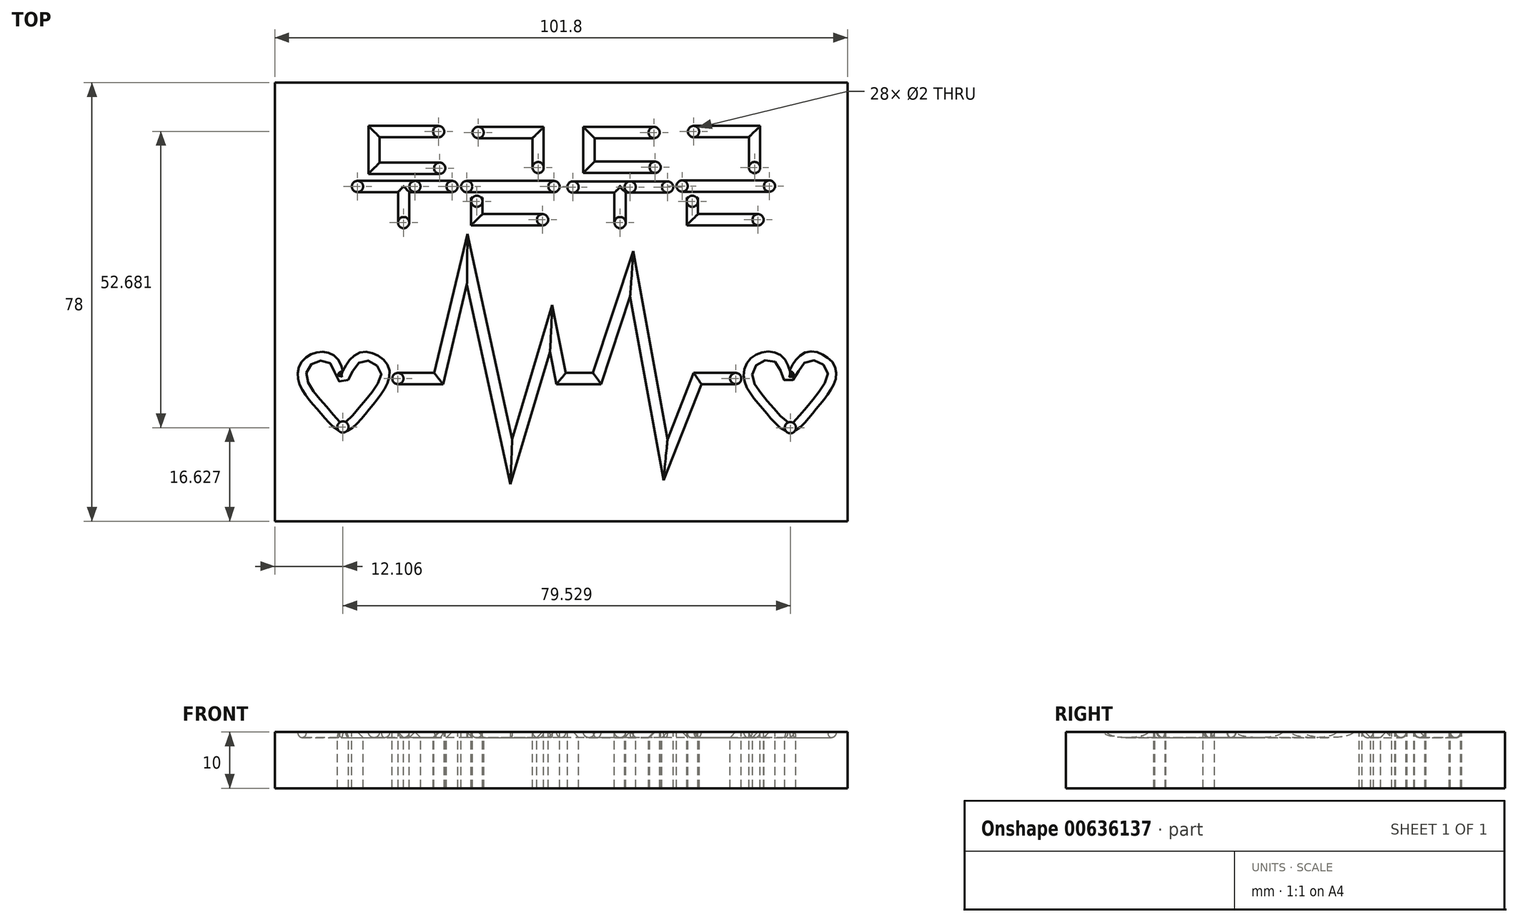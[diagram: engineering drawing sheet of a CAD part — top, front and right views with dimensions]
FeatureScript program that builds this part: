
annotation { "Feature Type Name" : "Feature", "Feature Type Description" : "" }
export const myFeature = defineFeature(function(context is Context, id is Id, definition is map)
    precondition{}
    {
        {
            var Q0;
            Q0=qCreatedBy(makeId("Top.planeOp"),FACE);
            var sketch = newSketch(context, id + "F0", { "sketchPlane" : qUnion([Q0])});
            skLineSegment(sketch, "E0.bottom", {"start": v(50.9, 39) * mm, "end": v(-50.9, 39) * mm});
            skLineSegment(sketch, "E0.top", {"start": v(50.9, -39) * mm, "end": v(-50.9, -39) * mm});
            skLineSegment(sketch, "E0.left", {"start": v(50.9, 39) * mm, "end": v(50.9, -39) * mm});
            skLineSegment(sketch, "E0.right", {"start": v(-50.9, 39) * mm, "end": v(-50.9, -39) * mm});
            skPoint(sketch, "E0.middle", {"position": v(0, 0) * mm});
            skSolve(sketch);
        }
        {
            var Q0;
            Q0 = qSketchRegion(id + "F0", true);
            extrude(context, id + "F1", {"entities" : qUnion([Q0]), "oppositeDirection" : true, "depth" : 10 * mm, "offsetDistance" : 25 * mm});
        }
        {
            var Q0;
            Q0=makeQuery(id+"F1.opExtrude","CAP_FACE",FACE,{"disambiguationData":[OSD([sQuery(id+"F0.wireOp",EDGE,"E0.bottom"),sQuery(id+"F0.wireOp",EDGE,"E0.top"),sQuery(id+"F0.wireOp",EDGE,"E0.left"),sQuery(id+"F0.wireOp",EDGE,"E0.right")])],"isStart":true});
            var sketch = newSketch(context, id + "F2", { "sketchPlane" : qUnion([Q0])});
            skLineSegment(sketch, "E1", {"start": v(-29.02, -13.62) * mm, "end": v(-21.78, -13.62) * mm});
            skLineSegment(sketch, "E2", {"start": v(-21.78, -13.62) * mm, "end": v(-16.7, 7.62) * mm});
            skLineSegment(sketch, "E3", {"start": v(-16.7, 7.62) * mm, "end": v(-8.85, -28.4) * mm});
            skLineSegment(sketch, "E4", {"start": v(-8.85, -28.4) * mm, "end": v(-1.77, -4.7) * mm});
            skLineSegment(sketch, "E5", {"start": v(-1.77, -4.7) * mm, "end": v(0, -13.62) * mm});
            skLineSegment(sketch, "E6", {"start": v(0, -13.62) * mm, "end": v(6.39, -13.62) * mm});
            skLineSegment(sketch, "E7", {"start": v(6.39, -13.62) * mm, "end": v(12.55, 5) * mm});
            skLineSegment(sketch, "E8", {"start": v(12.55, 5) * mm, "end": v(18.55, -28.1) * mm});
            skLineSegment(sketch, "E9", {"start": v(18.55, -28.1) * mm, "end": v(24.25, -13.62) * mm});
            skLineSegment(sketch, "E10", {"start": v(24.25, -13.62) * mm, "end": v(31.02, -13.62) * mm});
            skSolve(sketch);
        }
        {
            var Q0;
            Q0=makeQuery(id+"F1.opExtrude","SWEPT_FACE",FACE,{"disambiguationData":[OSD([sQuery(id+"F0.wireOp",EDGE,"E0.right")])]});
            cPlane(context, id + "F3", {"entities" : qUnion([Q0]), "cplaneType" : CPlaneType.OFFSET, "offset" : 22.1 * mm, "oppositeDirection" : true, "width" : 150 * mm, "height" : 150 * mm});
        }
        {
            var Q0;
            Q0=qCreatedBy(id+"F3.planeOp",FACE);
            var sketch = newSketch(context, id + "F4", { "sketchPlane" : qUnion([Q0])});
            skCircle(sketch, "E11", {"center": v(13.63, 0) * mm, "radius": 1 * mm});
            skSolve(sketch);
        }
        {
            var Q0;
            Q0=makeQuery(id+"F4.imprint","IMPRINT",FACE,{"disambiguationData":[TD([[makeQuery(id+"F4.imprint","IMPRINT",EDGE,{"derivedFrom":sQuery(id+"F4.wireOp",EDGE,"E11")}),1.0]])]});
            var Q1;
            Q1=sQuery(id+"F2.wireOp",EDGE,"E1");
            var Q2;
            Q2=sQuery(id+"F2.wireOp",EDGE,"E2");
            var Q3;
            Q3=sQuery(id+"F2.wireOp",EDGE,"E3");
            var Q4;
            Q4=sQuery(id+"F2.wireOp",EDGE,"E4");
            var Q5;
            Q5=sQuery(id+"F2.wireOp",EDGE,"E5");
            var Q6;
            Q6=sQuery(id+"F2.wireOp",EDGE,"E6");
            var Q7;
            Q7=sQuery(id+"F2.wireOp",EDGE,"E7");
            var Q8;
            Q8=sQuery(id+"F2.wireOp",EDGE,"E8");
            var Q9;
            Q9=sQuery(id+"F2.wireOp",EDGE,"E9");
            var Q10;
            Q10=sQuery(id+"F2.wireOp",EDGE,"E10");
            sweep(context, id + "F5", {"operationType" : NewBodyOperationType.REMOVE, "profiles" : qUnion([Q0]), "path" : qUnion([Q1, Q2, Q3, Q4, Q5, Q6, Q7, Q8, Q9, Q10])});
        }
        {
            var Q0;
            Q0=makeQuery(id+"F1.opExtrude","CAP_FACE",FACE,{"disambiguationData":[OSD([sQuery(id+"F0.wireOp",EDGE,"E0.bottom"),sQuery(id+"F0.wireOp",EDGE,"E0.top"),sQuery(id+"F0.wireOp",EDGE,"E0.left"),sQuery(id+"F0.wireOp",EDGE,"E0.right")])],"isStart":true});
            var sketch = newSketch(context, id + "F6", { "sketchPlane" : qUnion([Q0])});
            skLineSegment(sketch, "E12", {"start": v(-33.15, 30.19) * mm, "end": v(-21.78, 30.19) * mm});
            skLineSegment(sketch, "E13", {"start": v(-33.15, 30.19) * mm, "end": v(-33.15, 23.9) * mm});
            skLineSegment(sketch, "E14", {"start": v(-33.15, 23.9) * mm, "end": v(-21.6, 23.9) * mm});
            skLineSegment(sketch, "E15", {"start": v(-36.19, 20.58) * mm, "end": v(-19.38, 20.58) * mm});
            skLineSegment(sketch, "E16", {"start": v(-27.78, 20.58) * mm, "end": v(-27.78, 14.11) * mm});
            skLineSegment(sketch, "E17", {"start": v(-16.79, 20.58) * mm, "end": v(-1.27, 20.58) * mm});
            skLineSegment(sketch, "E18", {"start": v(-14.94, 18.55) * mm, "end": v(-14.94, 14.67) * mm});
            skLineSegment(sketch, "E19", {"start": v(-14.94, 14.67) * mm, "end": v(-3.3, 14.67) * mm});
            skLineSegment(sketch, "E20", {"start": v(-14.76, 30.19) * mm, "end": v(-4.04, 30.19) * mm});
            skLineSegment(sketch, "E21", {"start": v(-4.04, 30.19) * mm, "end": v(-4.04, 23.9) * mm});
            skLineSegment(sketch, "E22", {"start": v(4.88, 30.19) * mm, "end": v(16.52, 30.19) * mm});
            skLineSegment(sketch, "E23", {"start": v(4.88, 30.19) * mm, "end": v(4.88, 23.9) * mm});
            skLineSegment(sketch, "E24", {"start": v(4.88, 23.9) * mm, "end": v(16.7, 23.9) * mm});
            skLineSegment(sketch, "E25", {"start": v(2.1, 20.58) * mm, "end": v(18.92, 20.58) * mm});
            skLineSegment(sketch, "E26", {"start": v(10.51, 20.58) * mm, "end": v(10.51, 14.11) * mm});
            skLineSegment(sketch, "E27", {"start": v(21.5, 20.58) * mm, "end": v(37.02, 20.58) * mm});
            skLineSegment(sketch, "E28", {"start": v(23.35, 18.55) * mm, "end": v(23.35, 14.67) * mm});
            skLineSegment(sketch, "E29", {"start": v(23.35, 14.67) * mm, "end": v(35, 14.67) * mm});
            skLineSegment(sketch, "E30", {"start": v(23.54, 30.19) * mm, "end": v(34.25, 30.19) * mm});
            skLineSegment(sketch, "E31", {"start": v(34.25, 30.19) * mm, "end": v(34.25, 23.9) * mm});
            skSolve(sketch);
        }
        {
            var Q0;
            Q0=makeQuery(id+"F1.opExtrude","SWEPT_FACE",FACE,{"disambiguationData":[OSD([sQuery(id+"F0.wireOp",EDGE,"E0.right")])]});
            cPlane(context, id + "F7", {"entities" : qUnion([Q0]), "cplaneType" : CPlaneType.OFFSET, "offset" : 14.7 * mm, "oppositeDirection" : true, "width" : 150 * mm, "height" : 150 * mm});
        }
        {
            var Q0;
            Q0=qCreatedBy(id+"F7.planeOp",FACE);
            var sketch = newSketch(context, id + "F8", { "sketchPlane" : qUnion([Q0])});
            skCircle(sketch, "E32", {"center": v(-20.53, 0) * mm, "radius": 1 * mm});
            skSolve(sketch);
        }
        {
            var Q0;
            Q0=makeQuery(id+"F8.imprint","IMPRINT",FACE,{"disambiguationData":[TD([[makeQuery(id+"F8.imprint","IMPRINT",EDGE,{"derivedFrom":sQuery(id+"F8.wireOp",EDGE,"E32")}),1.0]])]});
            var Q1;
            Q1=sQuery(id+"F6.wireOp",EDGE,"E15");
            sweep(context, id + "F9", {"operationType" : NewBodyOperationType.REMOVE, "profiles" : qUnion([Q0]), "path" : qUnion([Q1])});
        }
        {
            var Q0;
            Q0=makeQuery(id+"F1.opExtrude","SWEPT_FACE",FACE,{"disambiguationData":[OSD([sQuery(id+"F0.wireOp",EDGE,"E0.right")])]});
            cPlane(context, id + "F10", {"entities" : qUnion([Q0]), "cplaneType" : CPlaneType.OFFSET, "offset" : 34.4 * mm, "oppositeDirection" : true, "width" : 150 * mm, "height" : 150 * mm});
        }
        {
            var Q0;
            Q0=qCreatedBy(id+"F10.planeOp",FACE);
            var sketch = newSketch(context, id + "F11", { "sketchPlane" : qUnion([Q0])});
            skCircle(sketch, "E33", {"center": v(-20.52, 0) * mm, "radius": 1 * mm});
            skSolve(sketch);
        }
        {
            var Q0;
            Q0=makeQuery(id+"F11.imprint","IMPRINT",FACE,{"disambiguationData":[TD([[makeQuery(id+"F11.imprint","IMPRINT",EDGE,{"derivedFrom":sQuery(id+"F11.wireOp",EDGE,"E33")}),1.0]])]});
            var Q1;
            Q1=sQuery(id+"F6.wireOp",EDGE,"E17");
            sweep(context, id + "F12", {"operationType" : NewBodyOperationType.REMOVE, "profiles" : qUnion([Q0]), "path" : qUnion([Q1])});
        }
        {
            var Q0;
            Q0=makeQuery(id+"F1.opExtrude","SWEPT_FACE",FACE,{"disambiguationData":[OSD([sQuery(id+"F0.wireOp",EDGE,"E0.right")])]});
            cPlane(context, id + "F13", {"entities" : qUnion([Q0]), "cplaneType" : CPlaneType.OFFSET, "offset" : 53.2 * mm, "oppositeDirection" : true, "width" : 150 * mm, "height" : 150 * mm});
        }
        {
            var Q0;
            Q0=qCreatedBy(id+"F13.planeOp",FACE);
            var sketch = newSketch(context, id + "F14", { "sketchPlane" : qUnion([Q0])});
            skCircle(sketch, "E34", {"center": v(-20.44, 0) * mm, "radius": 1 * mm});
            skSolve(sketch);
        }
        {
            var Q0;
            Q0=makeQuery(id+"F14.imprint","IMPRINT",FACE,{"disambiguationData":[TD([[makeQuery(id+"F14.imprint","IMPRINT",EDGE,{"derivedFrom":sQuery(id+"F14.wireOp",EDGE,"E34")}),1.0]])]});
            var Q1;
            Q1=sQuery(id+"F6.wireOp",EDGE,"E25");
            sweep(context, id + "F15", {"operationType" : NewBodyOperationType.REMOVE, "profiles" : qUnion([Q0]), "path" : qUnion([Q1])});
        }
        {
            var Q0;
            Q0=makeQuery(id+"F1.opExtrude","SWEPT_FACE",FACE,{"disambiguationData":[OSD([sQuery(id+"F0.wireOp",EDGE,"E0.right")])]});
            cPlane(context, id + "F16", {"entities" : qUnion([Q0]), "cplaneType" : CPlaneType.OFFSET, "offset" : 72.5 * mm, "oppositeDirection" : true, "width" : 150 * mm, "height" : 150 * mm});
        }
        {
            var Q0;
            Q0=qCreatedBy(id+"F16.planeOp",FACE);
            var sketch = newSketch(context, id + "F17", { "sketchPlane" : qUnion([Q0])});
            skCircle(sketch, "E35", {"center": v(-20.6, 0) * mm, "radius": 1 * mm});
            skSolve(sketch);
        }
        {
            var Q0;
            Q0=makeQuery(id+"F17.imprint","IMPRINT",FACE,{"disambiguationData":[TD([[makeQuery(id+"F17.imprint","IMPRINT",EDGE,{"derivedFrom":sQuery(id+"F17.wireOp",EDGE,"E35")}),1.0]])]});
            var Q1;
            Q1=sQuery(id+"F6.wireOp",EDGE,"E27");
            sweep(context, id + "F18", {"operationType" : NewBodyOperationType.REMOVE, "profiles" : qUnion([Q0]), "path" : qUnion([Q1])});
        }
        {
            var Q0;
            Q0=makeQuery(id+"F1.opExtrude","SWEPT_FACE",FACE,{"disambiguationData":[OSD([sQuery(id+"F0.wireOp",EDGE,"E0.bottom")])]});
            cPlane(context, id + "F19", {"entities" : qUnion([Q0]), "cplaneType" : CPlaneType.OFFSET, "offset" : 24.4 * mm, "oppositeDirection" : true, "width" : 150 * mm, "height" : 150 * mm});
        }
        {
            var Q0;
            Q0=qCreatedBy(id+"F19.planeOp",FACE);
            var sketch = newSketch(context, id + "F20", { "sketchPlane" : qUnion([Q0])});
            skCircle(sketch, "E36", {"center": v(28, 0) * mm, "radius": 1 * mm});
            skCircle(sketch, "E37", {"center": v(14.89, 0) * mm, "radius": 1 * mm});
            skCircle(sketch, "E38", {"center": v(-10.47, 0) * mm, "radius": 1 * mm});
            skCircle(sketch, "E39", {"center": v(-23.22, 0) * mm, "radius": 1 * mm});
            skSolve(sketch);
        }
        {
            var Q0;
            Q0=makeQuery(id+"F20.imprint","IMPRINT",FACE,{"disambiguationData":[TD([[makeQuery(id+"F20.imprint","IMPRINT",EDGE,{"derivedFrom":sQuery(id+"F20.wireOp",EDGE,"E36")}),1.0]])]});
            var Q1;
            Q1=sQuery(id+"F6.wireOp",EDGE,"E16");
            sweep(context, id + "F21", {"operationType" : NewBodyOperationType.REMOVE, "profiles" : qUnion([Q0]), "path" : qUnion([Q1])});
        }
        {
            var Q0;
            Q0=makeQuery(id+"F20.imprint","IMPRINT",FACE,{"disambiguationData":[TD([[makeQuery(id+"F20.imprint","IMPRINT",EDGE,{"derivedFrom":sQuery(id+"F20.wireOp",EDGE,"E38")}),1.0]])]});
            var Q1;
            Q1=sQuery(id+"F6.wireOp",EDGE,"E26");
            sweep(context, id + "F22", {"operationType" : NewBodyOperationType.REMOVE, "profiles" : qUnion([Q0]), "path" : qUnion([Q1])});
        }
        {
            var Q0;
            Q0=makeQuery(id+"F1.opExtrude","SWEPT_FACE",FACE,{"disambiguationData":[OSD([sQuery(id+"F0.wireOp",EDGE,"E0.left")])]});
            cPlane(context, id + "F23", {"entities" : qUnion([Q0]), "cplaneType" : CPlaneType.OFFSET, "offset" : 16.7 * mm, "oppositeDirection" : true, "width" : 150 * mm, "height" : 150 * mm});
        }
        {
            var Q0;
            Q0=qCreatedBy(id+"F23.planeOp",FACE);
            var sketch = newSketch(context, id + "F24", { "sketchPlane" : qUnion([Q0])});
            skCircle(sketch, "E40", {"center": v(14.62, 0) * mm, "radius": 1 * mm});
            skCircle(sketch, "E41", {"center": v(30.3, 0) * mm, "radius": 1 * mm});
            skSolve(sketch);
        }
        {
            var Q0;
            Q0=makeQuery(id+"F24.imprint","IMPRINT",FACE,{"disambiguationData":[TD([[makeQuery(id+"F24.imprint","IMPRINT",EDGE,{"derivedFrom":sQuery(id+"F24.wireOp",EDGE,"E40")}),1.0]])]});
            var Q1;
            Q1=sQuery(id+"F6.wireOp",EDGE,"E29");
            var Q2;
            Q2=sQuery(id+"F6.wireOp",EDGE,"E28");
            sweep(context, id + "F25", {"operationType" : NewBodyOperationType.REMOVE, "profiles" : qUnion([Q0]), "path" : qUnion([Q1, Q2])});
        }
        {
            var Q0;
            Q0=makeQuery(id+"F1.opExtrude","SWEPT_FACE",FACE,{"disambiguationData":[OSD([sQuery(id+"F0.wireOp",EDGE,"E0.left")])]});
            cPlane(context, id + "F26", {"entities" : qUnion([Q0]), "cplaneType" : CPlaneType.OFFSET, "offset" : 54.6 * mm, "oppositeDirection" : true, "width" : 150 * mm, "height" : 150 * mm});
        }
        {
            var Q0;
            Q0=qCreatedBy(id+"F26.planeOp",FACE);
            var sketch = newSketch(context, id + "F27", { "sketchPlane" : qUnion([Q0])});
            skCircle(sketch, "E42", {"center": v(14.62, 0) * mm, "radius": 1 * mm});
            skSolve(sketch);
        }
        {
            var Q0;
            Q0=makeQuery(id+"F27.imprint","IMPRINT",FACE,{"disambiguationData":[TD([[makeQuery(id+"F27.imprint","IMPRINT",EDGE,{"derivedFrom":sQuery(id+"F27.wireOp",EDGE,"E42")}),1.0]])]});
            var Q1;
            Q1=sQuery(id+"F6.wireOp",EDGE,"E19");
            var Q2;
            Q2=sQuery(id+"F6.wireOp",EDGE,"E18");
            sweep(context, id + "F28", {"operationType" : NewBodyOperationType.REMOVE, "profiles" : qUnion([Q0]), "path" : qUnion([Q1, Q2])});
        }
        {
            var Q0;
            Q0=makeQuery(id+"F1.opExtrude","SWEPT_FACE",FACE,{"disambiguationData":[OSD([sQuery(id+"F0.wireOp",EDGE,"E0.left")])]});
            cPlane(context, id + "F29", {"entities" : qUnion([Q0]), "cplaneType" : CPlaneType.OFFSET, "offset" : 25 * mm, "oppositeDirection" : true, "width" : 150 * mm, "height" : 150 * mm});
        }
        {
            var Q0;
            Q0=qCreatedBy(id+"F29.planeOp",FACE);
            var sketch = newSketch(context, id + "F30", { "sketchPlane" : qUnion([Q0])});
            skCircle(sketch, "E43", {"center": v(30.3, 0) * mm, "radius": 1 * mm});
            skSolve(sketch);
        }
        {
            var Q0;
            Q0=makeQuery(id+"F30.imprint","IMPRINT",FACE,{"disambiguationData":[TD([[makeQuery(id+"F30.imprint","IMPRINT",EDGE,{"derivedFrom":sQuery(id+"F30.wireOp",EDGE,"E43")}),1.0]])]});
            var Q1;
            Q1=sQuery(id+"F6.wireOp",EDGE,"E30");
            var Q2;
            Q2=sQuery(id+"F6.wireOp",EDGE,"E31");
            sweep(context, id + "F31", {"operationType" : NewBodyOperationType.REMOVE, "profiles" : qUnion([Q0]), "path" : qUnion([Q1, Q2])});
        }
        {
            var Q0;
            Q0=makeQuery(id+"F1.opExtrude","SWEPT_FACE",FACE,{"disambiguationData":[OSD([sQuery(id+"F0.wireOp",EDGE,"E0.left")])]});
            cPlane(context, id + "F32", {"entities" : qUnion([Q0]), "cplaneType" : CPlaneType.OFFSET, "offset" : 38.1 * mm, "oppositeDirection" : true, "width" : 150 * mm, "height" : 150 * mm});
        }
        {
            var Q0;
            Q0=qCreatedBy(id+"F32.planeOp",FACE);
            var sketch = newSketch(context, id + "F33", { "sketchPlane" : qUnion([Q0])});
            skCircle(sketch, "E44", {"center": v(30.13, 0) * mm, "radius": 1 * mm});
            skSolve(sketch);
        }
        {
            var Q0;
            Q0=makeQuery(id+"F33.imprint","IMPRINT",FACE,{"disambiguationData":[TD([[makeQuery(id+"F33.imprint","IMPRINT",EDGE,{"derivedFrom":sQuery(id+"F33.wireOp",EDGE,"E44")}),1.0]])]});
            var Q1;
            Q1=sQuery(id+"F6.wireOp",EDGE,"E22");
            var Q2;
            Q2=sQuery(id+"F6.wireOp",EDGE,"E23");
            var Q3;
            Q3=sQuery(id+"F6.wireOp",EDGE,"E24");
            sweep(context, id + "F34", {"operationType" : NewBodyOperationType.REMOVE, "profiles" : qUnion([Q0]), "path" : qUnion([Q1, Q2, Q3])});
        }
        {
            var Q0;
            Q0=makeQuery(id+"F1.opExtrude","SWEPT_FACE",FACE,{"disambiguationData":[OSD([sQuery(id+"F0.wireOp",EDGE,"E0.left")])]});
            cPlane(context, id + "F35", {"entities" : qUnion([Q0]), "cplaneType" : CPlaneType.OFFSET, "offset" : 63.9 * mm, "oppositeDirection" : true, "width" : 150 * mm, "height" : 150 * mm});
        }
        {
            var Q0;
            Q0=qCreatedBy(id+"F35.planeOp",FACE);
            var sketch = newSketch(context, id + "F36", { "sketchPlane" : qUnion([Q0])});
            skCircle(sketch, "E45", {"center": v(30.13, 0) * mm, "radius": 1 * mm});
            skSolve(sketch);
        }
        {
            var Q0;
            Q0=makeQuery(id+"F36.imprint","IMPRINT",FACE,{"disambiguationData":[TD([[makeQuery(id+"F36.imprint","IMPRINT",EDGE,{"derivedFrom":sQuery(id+"F36.wireOp",EDGE,"E45")}),1.0]])]});
            var Q1;
            Q1=sQuery(id+"F6.wireOp",EDGE,"E20");
            var Q2;
            Q2=sQuery(id+"F6.wireOp",EDGE,"E21");
            sweep(context, id + "F37", {"operationType" : NewBodyOperationType.REMOVE, "profiles" : qUnion([Q0]), "path" : qUnion([Q1, Q2])});
        }
        {
            var Q0;
            Q0=makeQuery(id+"F1.opExtrude","SWEPT_FACE",FACE,{"disambiguationData":[OSD([sQuery(id+"F0.wireOp",EDGE,"E0.left")])]});
            cPlane(context, id + "F38", {"entities" : qUnion([Q0]), "cplaneType" : CPlaneType.OFFSET, "offset" : 80.2 * mm, "oppositeDirection" : true, "width" : 150 * mm, "height" : 150 * mm});
        }
        {
            var Q0;
            Q0=qCreatedBy(id+"F38.planeOp",FACE);
            var sketch = newSketch(context, id + "F39", { "sketchPlane" : qUnion([Q0])});
            skCircle(sketch, "E46", {"center": v(30.3, 0) * mm, "radius": 1 * mm});
            skSolve(sketch);
        }
        {
            var Q0;
            Q0=makeQuery(id+"F39.imprint","IMPRINT",FACE,{"disambiguationData":[TD([[makeQuery(id+"F39.imprint","IMPRINT",EDGE,{"derivedFrom":sQuery(id+"F39.wireOp",EDGE,"E46")}),1.0]])]});
            var Q1;
            Q1=sQuery(id+"F6.wireOp",EDGE,"E12");
            var Q2;
            Q2=sQuery(id+"F6.wireOp",EDGE,"E13");
            var Q3;
            Q3=sQuery(id+"F6.wireOp",EDGE,"E14");
            sweep(context, id + "F40", {"operationType" : NewBodyOperationType.REMOVE, "profiles" : qUnion([Q0]), "path" : qUnion([Q1, Q2, Q3])});
        }
        {
            var Q0;
            Q0=makeQuery(id+"F1.opExtrude","CAP_FACE",FACE,{"disambiguationData":[OSD([sQuery(id+"F0.wireOp",EDGE,"E0.bottom"),sQuery(id+"F0.wireOp",EDGE,"E0.top"),sQuery(id+"F0.wireOp",EDGE,"E0.left"),sQuery(id+"F0.wireOp",EDGE,"E0.right")])],"isStart":true});
            var sketch = newSketch(context, id + "F41", { "sketchPlane" : qUnion([Q0])});
            skFitSpline(sketch, "E47", {"points": [v(-38.89, -13.4) * mm, v(-40, -11.18) * mm, v(-42.21, -9.7) * mm, v(-45.17, -10.8) * mm, v(-45.9, -13.95) * mm, v(-42.3, -19.14) * mm, v(-38.68, -22.16) * mm, v(-35.22, -19.25) * mm, v(-31.48, -13.87) * mm, v(-31.87, -11.17) * mm, v(-34.78, -9.7) * mm, v(-37.2, -11.12) * mm, v(-38.89, -13.4) * mm]});
            skFitSpline(sketch, "E48", {"points": [v(40.44, -13.4) * mm, v(39.33, -11.18) * mm, v(37.11, -9.7) * mm, v(34.16, -10.8) * mm, v(33.42, -13.95) * mm, v(37.02, -19.14) * mm, v(40.65, -22.16) * mm, v(44.1, -19.25) * mm, v(47.84, -13.87) * mm, v(47.46, -11.17) * mm, v(44.55, -9.7) * mm, v(42.13, -11.12) * mm, v(40.44, -13.4) * mm]});
            skSolve(sketch);
        }
        {
            var Q0;
            Q0=makeQuery(id+"F1.opExtrude","SWEPT_FACE",FACE,{"disambiguationData":[OSD([sQuery(id+"F0.wireOp",EDGE,"E0.top")])]});
            cPlane(context, id + "F42", {"entities" : qUnion([Q0]), "cplaneType" : CPlaneType.OFFSET, "offset" : 21.3 * mm, "oppositeDirection" : true, "width" : 150 * mm, "height" : 150 * mm});
        }
        {
            var Q0;
            Q0=qCreatedBy(id+"F42.planeOp",FACE);
            var sketch = newSketch(context, id + "F43", { "sketchPlane" : qUnion([Q0])});
            skCircle(sketch, "E49", {"center": v(-33.96, 0) * mm, "radius": 1 * mm});
            skSolve(sketch);
        }
        {
            var Q0;
            Q0=makeQuery(id+"F43.imprint","IMPRINT",FACE,{"disambiguationData":[TD([[makeQuery(id+"F43.imprint","IMPRINT",EDGE,{"derivedFrom":sQuery(id+"F43.wireOp",EDGE,"E49")}),1.0]])]});
            var Q1;
            Q1=sQuery(id+"F41.wireOp",EDGE,"E47");
            sweep(context, id + "F44", {"operationType" : NewBodyOperationType.REMOVE, "profiles" : qUnion([Q0]), "path" : qUnion([Q1])});
        }
        {
            var Q0;
            Q0=qCreatedBy(id+"F42.planeOp",FACE);
            var sketch = newSketch(context, id + "F45", { "sketchPlane" : qUnion([Q0])});
            skCircle(sketch, "E50", {"center": v(35.72, 0) * mm, "radius": 1 * mm});
            skSolve(sketch);
        }
        {
            var Q0;
            Q0=makeQuery(id+"F45.imprint","IMPRINT",FACE,{"disambiguationData":[TD([[makeQuery(id+"F45.imprint","IMPRINT",EDGE,{"derivedFrom":sQuery(id+"F45.wireOp",EDGE,"E50")}),1.0]])]});
            var Q1;
            Q1=sQuery(id+"F41.wireOp",EDGE,"E48");
            sweep(context, id + "F46", {"operationType" : NewBodyOperationType.REMOVE, "profiles" : qUnion([Q0]), "path" : qUnion([Q1])});
        }
        {
            var Q0;
            {var subQ0=sQuery(id+"F30.wireOp",EDGE,"E43");var subQ1=makeQuery(id+"F31.boolean.opBoolean","COPY",FACE,{"derivedFrom":makeQuery(id+"F31.opSweep","SWEPT_FACE",FACE,{"disambiguationData":[OSD([sQuery(id+"F6.wireOp",EDGE,"E31"),subQ0])]})});var subQ2=sQuery(id+"F11.wireOp",EDGE,"E33");var subQ3=makeQuery(id+"F12.boolean.opBoolean","COPY",FACE,{"derivedFrom":makeQuery(id+"F12.opSweep","CAP_FACE",FACE,{"disambiguationData":[OSD([sQuery(id+"F6.wireOp",VERTEX,"E17.end"),subQ2])],"isStart":true})});var subQ4=sQuery(id+"F27.wireOp",EDGE,"E42");var subQ5=makeQuery(id+"F28.boolean.opBoolean","COPY",FACE,{"derivedFrom":makeQuery(id+"F28.opSweep","SWEPT_FACE",FACE,{"disambiguationData":[OSD([sQuery(id+"F6.wireOp",EDGE,"E19"),subQ4])]})});var subQ6=sQuery(id+"F8.wireOp",EDGE,"E32");var subQ7=makeQuery(id+"F9.boolean.opBoolean","COPY",FACE,{"derivedFrom":makeQuery(id+"F9.opSweep","CAP_FACE",FACE,{"disambiguationData":[OSD([sQuery(id+"F6.wireOp",VERTEX,"E15.end"),subQ6])],"isStart":false})});var subQ8=makeQuery(id+"F28.boolean.opBoolean","COPY",FACE,{"derivedFrom":makeQuery(id+"F28.opSweep","SWEPT_FACE",FACE,{"disambiguationData":[OSD([sQuery(id+"F6.wireOp",EDGE,"E18"),subQ4])]})});var subQ9=makeQuery(id+"F9.boolean.opBoolean","COPY",FACE,{"derivedFrom":makeQuery(id+"F9.opSweep","CAP_FACE",FACE,{"disambiguationData":[OSD([sQuery(id+"F6.wireOp",VERTEX,"E15.start"),subQ6])],"isStart":true})});var subQ10=sQuery(id+"F0.wireOp",EDGE,"E0.right");var subQ11=sQuery(id+"F0.wireOp",EDGE,"E0.left");var subQ12=sQuery(id+"F0.wireOp",EDGE,"E0.top");var subQ13=sQuery(id+"F0.wireOp",EDGE,"E0.bottom");var subQ14=makeQuery(id+"F1.opExtrude","CAP_FACE",FACE,{"disambiguationData":[OSD([subQ13,subQ12,subQ11,subQ10])],"isStart":true});var subQ15=sQuery(id+"F14.wireOp",EDGE,"E34");var subQ16=makeQuery(id+"F15.boolean.opBoolean","COPY",FACE,{"derivedFrom":makeQuery(id+"F15.opSweep","SWEPT_FACE",FACE,{"disambiguationData":[OSD([sQuery(id+"F6.wireOp",EDGE,"E25"),subQ15])]})});var subQ17=sQuery(id+"F20.wireOp",EDGE,"E38");var subQ18=makeQuery(id+"F22.opSweep","CAP_FACE",FACE,{"disambiguationData":[OSD([sQuery(id+"F6.wireOp",VERTEX,"E26.end"),subQ17])],"isStart":true});var subQ19=makeQuery(id+"F22.opSweep","SWEPT_FACE",FACE,{"disambiguationData":[OSD([sQuery(id+"F6.wireOp",EDGE,"E26"),subQ17])]});var subQ20=makeQuery(id+"F22.boolean.opBoolean","COPY",FACE,{"disambiguationData":[TD([subQ18])],"derivedFrom":subQ19});var subQ21=makeQuery(id+"F31.boolean.opBoolean","COPY",FACE,{"derivedFrom":makeQuery(id+"F31.opSweep","SWEPT_FACE",FACE,{"disambiguationData":[OSD([sQuery(id+"F6.wireOp",EDGE,"E30"),subQ0])]})});var subQ22=makeQuery(id+"F12.boolean.opBoolean","COPY",FACE,{"derivedFrom":makeQuery(id+"F12.opSweep","CAP_FACE",FACE,{"disambiguationData":[OSD([sQuery(id+"F6.wireOp",VERTEX,"E17.start"),subQ2])],"isStart":false})});var subQ23=makeQuery(id+"F22.boolean.opBoolean","COPY",FACE,{"derivedFrom":subQ18});var subQ24=makeQuery(id+"F9.boolean.opBoolean","COPY",FACE,{"derivedFrom":makeQuery(id+"F9.opSweep","SWEPT_FACE",FACE,{"disambiguationData":[OSD([sQuery(id+"F6.wireOp",EDGE,"E15"),subQ6])]})});var subQ25=sQuery(id+"F20.wireOp",EDGE,"E36");var subQ26=makeQuery(id+"F21.opSweep","CAP_FACE",FACE,{"disambiguationData":[OSD([sQuery(id+"F6.wireOp",VERTEX,"E16.end"),subQ25])],"isStart":true});var subQ27=makeQuery(id+"F21.opSweep","SWEPT_FACE",FACE,{"disambiguationData":[OSD([sQuery(id+"F6.wireOp",EDGE,"E16"),subQ25])]});var subQ28=makeQuery(id+"F21.boolean.opBoolean","COPY",FACE,{"disambiguationData":[TD([subQ14,subQ24,subQ26,subQ27])],"derivedFrom":subQ27});var subQ29=sQuery(id+"F17.wireOp",EDGE,"E35");var subQ30=makeQuery(id+"F18.boolean.opBoolean","COPY",FACE,{"derivedFrom":makeQuery(id+"F18.opSweep","CAP_FACE",FACE,{"disambiguationData":[OSD([sQuery(id+"F6.wireOp",VERTEX,"E27.start"),subQ29])],"isStart":false})});var subQ31=sQuery(id+"F36.wireOp",EDGE,"E45");var subQ32=makeQuery(id+"F37.boolean.opBoolean","COPY",FACE,{"derivedFrom":makeQuery(id+"F37.opSweep","SWEPT_FACE",FACE,{"disambiguationData":[OSD([sQuery(id+"F6.wireOp",EDGE,"E20"),subQ31])]})});var subQ33=sQuery(id+"F33.wireOp",EDGE,"E44");var subQ34=makeQuery(id+"F34.boolean.opBoolean","COPY",FACE,{"derivedFrom":makeQuery(id+"F34.opSweep","CAP_FACE",FACE,{"disambiguationData":[OSD([sQuery(id+"F6.wireOp",VERTEX,"E24.end"),subQ33])],"isStart":true})});var subQ35=sQuery(id+"F4.wireOp",EDGE,"E11");var subQ36=makeQuery(id+"F5.boolean.opBoolean","COPY",FACE,{"derivedFrom":makeQuery(id+"F5.opSweep","SWEPT_FACE",FACE,{"disambiguationData":[OSD([sQuery(id+"F2.wireOp",EDGE,"E3"),subQ35])]})});var subQ37=sQuery(id+"F24.wireOp",EDGE,"E40");var subQ38=makeQuery(id+"F25.boolean.opBoolean","COPY",FACE,{"derivedFrom":makeQuery(id+"F25.opSweep","CAP_FACE",FACE,{"disambiguationData":[OSD([sQuery(id+"F6.wireOp",VERTEX,"E28.start"),subQ37])],"isStart":true})});var subQ39=makeQuery(id+"F5.boolean.opBoolean","COPY",FACE,{"derivedFrom":makeQuery(id+"F5.opSweep","SWEPT_FACE",FACE,{"disambiguationData":[OSD([sQuery(id+"F2.wireOp",EDGE,"E9"),subQ35])]})});var subQ40=makeQuery(id+"F5.boolean.opBoolean","COPY",FACE,{"derivedFrom":makeQuery(id+"F5.opSweep","SWEPT_FACE",FACE,{"disambiguationData":[OSD([sQuery(id+"F2.wireOp",EDGE,"E6"),subQ35])]})});var subQ41=makeQuery(id+"F34.boolean.opBoolean","COPY",FACE,{"derivedFrom":makeQuery(id+"F34.opSweep","SWEPT_FACE",FACE,{"disambiguationData":[OSD([sQuery(id+"F6.wireOp",EDGE,"E24"),subQ33])]})});var subQ42=makeQuery(id+"F34.boolean.opBoolean","COPY",FACE,{"derivedFrom":makeQuery(id+"F34.opSweep","CAP_FACE",FACE,{"disambiguationData":[OSD([sQuery(id+"F6.wireOp",VERTEX,"E22.end"),subQ33])],"isStart":false})});var subQ43=makeQuery(id+"F5.boolean.opBoolean","COPY",FACE,{"derivedFrom":makeQuery(id+"F5.opSweep","SWEPT_FACE",FACE,{"disambiguationData":[OSD([sQuery(id+"F2.wireOp",EDGE,"E2"),subQ35])]})});var subQ44=makeQuery(id+"F15.boolean.opBoolean","COPY",FACE,{"derivedFrom":makeQuery(id+"F15.opSweep","CAP_FACE",FACE,{"disambiguationData":[OSD([sQuery(id+"F6.wireOp",VERTEX,"E25.end"),subQ15])],"isStart":true})});var subQ45=makeQuery(id+"F5.boolean.opBoolean","COPY",FACE,{"derivedFrom":makeQuery(id+"F5.opSweep","SWEPT_FACE",FACE,{"disambiguationData":[OSD([sQuery(id+"F2.wireOp",EDGE,"E5"),subQ35])]})});var subQ46=makeQuery(id+"F34.boolean.opBoolean","COPY",FACE,{"derivedFrom":makeQuery(id+"F34.opSweep","SWEPT_FACE",FACE,{"disambiguationData":[OSD([sQuery(id+"F6.wireOp",EDGE,"E23"),subQ33])]})});var subQ47=makeQuery(id+"F15.boolean.opBoolean","COPY",FACE,{"derivedFrom":makeQuery(id+"F15.opSweep","CAP_FACE",FACE,{"disambiguationData":[OSD([sQuery(id+"F6.wireOp",VERTEX,"E25.start"),subQ15])],"isStart":false})});var subQ48=makeQuery(id+"F5.boolean.opBoolean","COPY",FACE,{"derivedFrom":makeQuery(id+"F5.opSweep","SWEPT_FACE",FACE,{"disambiguationData":[OSD([sQuery(id+"F2.wireOp",EDGE,"E4"),subQ35])]})});var subQ49=makeQuery(id+"F34.boolean.opBoolean","COPY",FACE,{"derivedFrom":makeQuery(id+"F34.opSweep","SWEPT_FACE",FACE,{"disambiguationData":[OSD([sQuery(id+"F6.wireOp",EDGE,"E22"),subQ33])]})});var subQ50=makeQuery(id+"F5.boolean.opBoolean","COPY",FACE,{"derivedFrom":makeQuery(id+"F5.opSweep","SWEPT_FACE",FACE,{"disambiguationData":[OSD([sQuery(id+"F2.wireOp",EDGE,"E1"),subQ35])]})});var subQ51=makeQuery(id+"F5.boolean.opBoolean","COPY",FACE,{"derivedFrom":makeQuery(id+"F5.opSweep","CAP_FACE",FACE,{"disambiguationData":[OSD([sQuery(id+"F2.wireOp",VERTEX,"E10.end"),subQ35])],"isStart":true})});var subQ52=makeQuery(id+"F5.boolean.opBoolean","COPY",FACE,{"derivedFrom":makeQuery(id+"F5.opSweep","CAP_FACE",FACE,{"disambiguationData":[OSD([sQuery(id+"F2.wireOp",VERTEX,"E1.start"),subQ35])],"isStart":false})});var subQ53=makeQuery(id+"F25.boolean.opBoolean","COPY",FACE,{"derivedFrom":makeQuery(id+"F25.opSweep","CAP_FACE",FACE,{"disambiguationData":[OSD([sQuery(id+"F6.wireOp",VERTEX,"E29.end"),subQ37])],"isStart":false})});var subQ54=makeQuery(id+"F5.boolean.opBoolean","COPY",FACE,{"derivedFrom":makeQuery(id+"F5.opSweep","SWEPT_FACE",FACE,{"disambiguationData":[OSD([sQuery(id+"F2.wireOp",EDGE,"E10"),subQ35])]})});var subQ55=makeQuery(id+"F1.opExtrude","SWEPT_FACE",FACE,{"disambiguationData":[OSD([subQ13])]});var subQ56=makeQuery(id+"F25.boolean.opBoolean","COPY",FACE,{"derivedFrom":makeQuery(id+"F25.opSweep","SWEPT_FACE",FACE,{"disambiguationData":[OSD([sQuery(id+"F6.wireOp",EDGE,"E28"),subQ37])]})});var subQ57=makeQuery(id+"F1.opExtrude","SWEPT_FACE",FACE,{"disambiguationData":[OSD([subQ12])]});var subQ58=makeQuery(id+"F5.boolean.opBoolean","COPY",FACE,{"derivedFrom":makeQuery(id+"F5.opSweep","SWEPT_FACE",FACE,{"disambiguationData":[OSD([sQuery(id+"F2.wireOp",EDGE,"E8"),subQ35])]})});var subQ59=makeQuery(id+"F21.boolean.opBoolean","COPY",FACE,{"derivedFrom":subQ26});var subQ60=sQuery(id+"F39.wireOp",EDGE,"E46");var subQ61=makeQuery(id+"F40.boolean.opBoolean","COPY",FACE,{"derivedFrom":makeQuery(id+"F40.opSweep","SWEPT_FACE",FACE,{"disambiguationData":[OSD([sQuery(id+"F6.wireOp",EDGE,"E12"),subQ60])]})});var subQ62=makeQuery(id+"F1.opExtrude","SWEPT_FACE",FACE,{"disambiguationData":[OSD([subQ11])]});var subQ63=makeQuery(id+"F25.boolean.opBoolean","COPY",FACE,{"derivedFrom":makeQuery(id+"F25.opSweep","SWEPT_FACE",FACE,{"disambiguationData":[OSD([sQuery(id+"F6.wireOp",EDGE,"E29"),subQ37])]})});var subQ64=makeQuery(id+"F5.boolean.opBoolean","COPY",FACE,{"derivedFrom":makeQuery(id+"F5.opSweep","SWEPT_FACE",FACE,{"disambiguationData":[OSD([sQuery(id+"F2.wireOp",EDGE,"E7"),subQ35])]})});var subQ65=makeQuery(id+"F44.opSweep","SWEPT_FACE",FACE,{"disambiguationData":[OSD([sQuery(id+"F41.wireOp",EDGE,"E47"),sQuery(id+"F43.wireOp",EDGE,"E49")])]});var subQ66=makeQuery(id+"F18.boolean.opBoolean","COPY",FACE,{"derivedFrom":makeQuery(id+"F18.opSweep","CAP_FACE",FACE,{"disambiguationData":[OSD([sQuery(id+"F6.wireOp",VERTEX,"E27.end"),subQ29])],"isStart":true})});var subQ67=makeQuery(id+"F37.boolean.opBoolean","COPY",FACE,{"derivedFrom":makeQuery(id+"F37.opSweep","SWEPT_FACE",FACE,{"disambiguationData":[OSD([sQuery(id+"F6.wireOp",EDGE,"E21"),subQ31])]})});var subQ68=makeQuery(id+"F31.boolean.opBoolean","COPY",FACE,{"derivedFrom":makeQuery(id+"F31.opSweep","CAP_FACE",FACE,{"disambiguationData":[OSD([sQuery(id+"F6.wireOp",VERTEX,"E30.start"),subQ0])],"isStart":true})});var subQ69=makeQuery(id+"F28.boolean.opBoolean","COPY",FACE,{"derivedFrom":makeQuery(id+"F28.opSweep","CAP_FACE",FACE,{"disambiguationData":[OSD([sQuery(id+"F6.wireOp",VERTEX,"E18.start"),subQ4])],"isStart":true})});var subQ70=makeQuery(id+"F18.boolean.opBoolean","COPY",FACE,{"derivedFrom":makeQuery(id+"F18.opSweep","SWEPT_FACE",FACE,{"disambiguationData":[OSD([sQuery(id+"F6.wireOp",EDGE,"E27"),subQ29])]})});var subQ71=makeQuery(id+"F31.boolean.opBoolean","COPY",FACE,{"derivedFrom":makeQuery(id+"F31.opSweep","CAP_FACE",FACE,{"disambiguationData":[OSD([sQuery(id+"F6.wireOp",VERTEX,"E31.end"),subQ0])],"isStart":false})});var subQ72=makeQuery(id+"F12.boolean.opBoolean","COPY",FACE,{"derivedFrom":makeQuery(id+"F12.opSweep","SWEPT_FACE",FACE,{"disambiguationData":[OSD([sQuery(id+"F6.wireOp",EDGE,"E17"),subQ2])]})});var subQ73=makeQuery(id+"F28.boolean.opBoolean","COPY",FACE,{"derivedFrom":makeQuery(id+"F28.opSweep","CAP_FACE",FACE,{"disambiguationData":[OSD([sQuery(id+"F6.wireOp",VERTEX,"E19.end"),subQ4])],"isStart":false})});var subQ74=makeQuery(id+"F1.opExtrude","SWEPT_FACE",FACE,{"disambiguationData":[OSD([subQ10])]});var subQ75=makeQuery(id+"F37.boolean.opBoolean","COPY",FACE,{"derivedFrom":makeQuery(id+"F37.opSweep","CAP_FACE",FACE,{"disambiguationData":[OSD([sQuery(id+"F6.wireOp",VERTEX,"E20.start"),subQ31])],"isStart":true})});var subQ76=makeQuery(id+"F37.boolean.opBoolean","COPY",FACE,{"derivedFrom":makeQuery(id+"F37.opSweep","CAP_FACE",FACE,{"disambiguationData":[OSD([sQuery(id+"F6.wireOp",VERTEX,"E21.end"),subQ31])],"isStart":false})});var subQ77=makeQuery(id+"F40.boolean.opBoolean","COPY",FACE,{"derivedFrom":makeQuery(id+"F40.opSweep","CAP_FACE",FACE,{"disambiguationData":[OSD([sQuery(id+"F6.wireOp",VERTEX,"E12.end"),subQ60])],"isStart":false})});var subQ78=makeQuery(id+"F40.boolean.opBoolean","COPY",FACE,{"derivedFrom":makeQuery(id+"F40.opSweep","CAP_FACE",FACE,{"disambiguationData":[OSD([sQuery(id+"F6.wireOp",VERTEX,"E14.end"),subQ60])],"isStart":true})});var subQ79=makeQuery(id+"F40.boolean.opBoolean","COPY",FACE,{"derivedFrom":makeQuery(id+"F40.opSweep","SWEPT_FACE",FACE,{"disambiguationData":[OSD([sQuery(id+"F6.wireOp",EDGE,"E13"),subQ60])]})});var subQ80=makeQuery(id+"F40.boolean.opBoolean","COPY",FACE,{"derivedFrom":makeQuery(id+"F40.opSweep","SWEPT_FACE",FACE,{"disambiguationData":[OSD([sQuery(id+"F6.wireOp",EDGE,"E14"),subQ60])]})});Q0=makeQuery(id+"F46.boolean.opBoolean","SPLIT",FACE,{"disambiguationData":[TD([subQ55,subQ57,subQ62,subQ74,subQ52,subQ51,subQ50,subQ43,subQ36,subQ48,subQ45,subQ40,subQ64,subQ58,subQ39,subQ54,subQ9,subQ7,subQ24,subQ22,subQ3,subQ72,subQ47,subQ44,subQ16,subQ30,subQ66,subQ70,subQ59,subQ28,subQ23,subQ20,subQ38,subQ53,subQ56,subQ63,subQ69,subQ73,subQ8,subQ5,subQ68,subQ71,subQ21,subQ1,subQ42,subQ34,subQ49,subQ46,subQ41,subQ75,subQ76,subQ32,subQ67,subQ77,subQ78,subQ61,subQ79,subQ80,makeQuery(id+"F44.boolean.opBoolean","COPY",FACE,{"derivedFrom":subQ65}),makeQuery(id+"F46.opSweep","SWEPT_FACE",FACE,{"disambiguationData":[OSD([sQuery(id+"F41.wireOp",EDGE,"E48"),sQuery(id+"F45.wireOp",EDGE,"E50")])]})])],"derivedFrom":makeQuery(id+"F44.boolean.opBoolean","SPLIT",FACE,{"disambiguationData":[TD([subQ55,subQ57,subQ62,subQ74,subQ52,subQ51,subQ50,subQ43,subQ36,subQ48,subQ45,subQ40,subQ64,subQ58,subQ39,subQ54,subQ9,subQ7,subQ24,subQ22,subQ3,subQ72,subQ47,subQ44,subQ16,subQ30,subQ66,subQ70,subQ59,subQ28,subQ23,subQ20,subQ38,subQ53,subQ56,subQ63,subQ69,subQ73,subQ8,subQ5,subQ68,subQ71,subQ21,subQ1,subQ42,subQ34,subQ49,subQ46,subQ41,subQ75,subQ76,subQ32,subQ67,subQ77,subQ78,subQ61,subQ79,subQ80,subQ65])],"derivedFrom":subQ14})});}
            var sketch = newSketch(context, id + "F47", { "sketchPlane" : qUnion([Q0])});
            skCircle(sketch, "E51", {"center": v(-38.8, -22.24) * mm, "radius": 1 * mm});
            skCircle(sketch, "E52", {"center": v(-29.02, -13.63) * mm, "radius": 1 * mm});
            skCircle(sketch, "E53", {"center": v(31.02, -13.63) * mm, "radius": 1 * mm});
            skCircle(sketch, "E54", {"center": v(40.73, -22.37) * mm, "radius": 1 * mm});
            skCircle(sketch, "E55", {"center": v(-21.78, 30.3) * mm, "radius": 1 * mm});
            skCircle(sketch, "E56", {"center": v(-21.6, 23.79) * mm, "radius": 1 * mm});
            skCircle(sketch, "E57", {"center": v(-14.76, 30.13) * mm, "radius": 1 * mm});
            skCircle(sketch, "E58", {"center": v(-19.39, 20.53) * mm, "radius": 1 * mm});
            skCircle(sketch, "E59", {"center": v(-36.2, 20.53) * mm, "radius": 1 * mm});
            skCircle(sketch, "E60", {"center": v(-28, 14.11) * mm, "radius": 1 * mm});
            skCircle(sketch, "E61", {"center": v(-26, 20.53) * mm, "radius": 1 * mm});
            skCircle(sketch, "E62", {"center": v(-4.1, 23.9) * mm, "radius": 1 * mm});
            skCircle(sketch, "E63", {"center": v(-16.79, 20.52) * mm, "radius": 1 * mm});
            skCircle(sketch, "E64", {"center": v(-1.27, 20.52) * mm, "radius": 1 * mm});
            skCircle(sketch, "E65", {"center": v(-14.99, 17.9) * mm, "radius": 1 * mm});
            skCircle(sketch, "E66", {"center": v(-3.3, 14.62) * mm, "radius": 1 * mm});
            skCircle(sketch, "E67", {"center": v(16.52, 30.13) * mm, "radius": 1 * mm});
            skCircle(sketch, "E68", {"center": v(16.7, 23.96) * mm, "radius": 1 * mm});
            skCircle(sketch, "E69", {"center": v(2.1, 20.44) * mm, "radius": 1 * mm});
            skCircle(sketch, "E70", {"center": v(10.47, 14.11) * mm, "radius": 1 * mm});
            skCircle(sketch, "E71", {"center": v(12.26, 20.44) * mm, "radius": 1 * mm});
            skCircle(sketch, "E72", {"center": v(18.92, 20.44) * mm, "radius": 1 * mm});
            skCircle(sketch, "E73", {"center": v(23.54, 30.3) * mm, "radius": 1 * mm});
            skCircle(sketch, "E74", {"center": v(34.37, 23.9) * mm, "radius": 1 * mm});
            skCircle(sketch, "E75", {"center": v(21.5, 20.6) * mm, "radius": 1 * mm});
            skCircle(sketch, "E76", {"center": v(37.02, 20.6) * mm, "radius": 1 * mm});
            skCircle(sketch, "E77", {"center": v(23.3, 17.9) * mm, "radius": 1 * mm});
            skCircle(sketch, "E78", {"center": v(35, 14.62) * mm, "radius": 1 * mm});
            skSolve(sketch);
        }
        {
            var Q0;
            Q0 = qSketchRegion(id + "F47", true);
            extrude(context, id + "F48", {"entities" : qUnion([Q0]), "operationType" : NewBodyOperationType.REMOVE, "oppositeDirection" : true, "depth" : 25 * mm, "offsetDistance" : 25 * mm});
        }
    });
